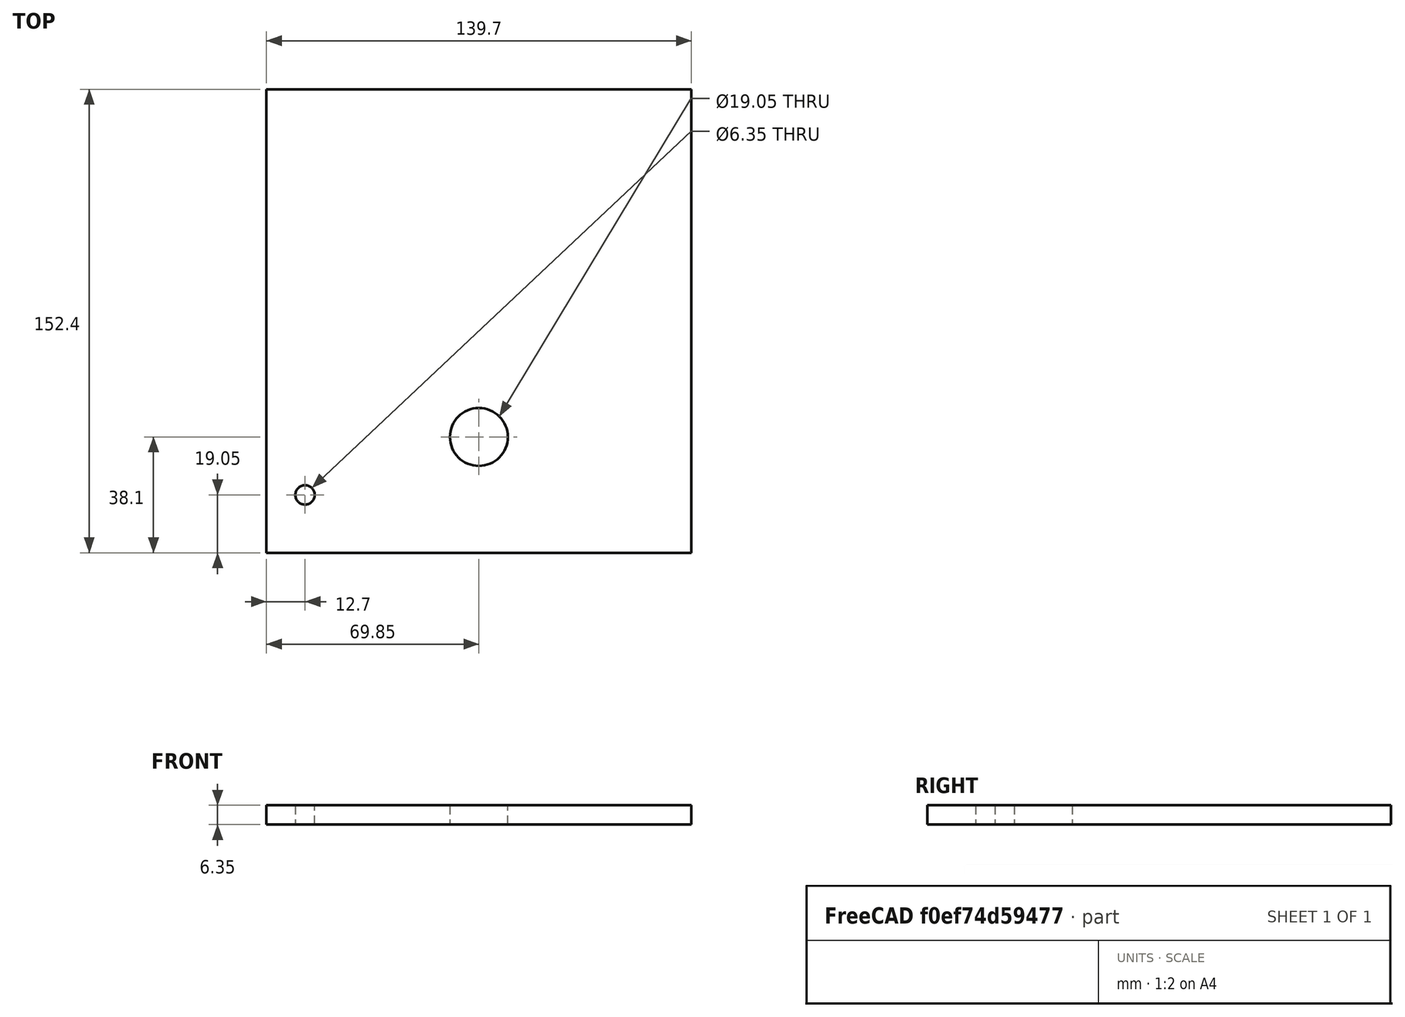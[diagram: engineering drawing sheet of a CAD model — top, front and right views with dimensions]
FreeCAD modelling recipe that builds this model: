
FCSTD DOCUMENT  (FreeCAD 0.22R36784 (Git))
Label: fiat 125 battery cutoff switch plate
License: All rights reserved
LicenseURL: http://en.wikipedia.org/wiki/All_rights_reserved
objects: Sketcher::SketchObject×1, PartDesign::Pad×1, PartDesign::Body×1
note: 4 computed .brp shape members not serialized (recipe doc carries the construction recipe); baked Part::Feature solids carry a one-line shape summary decoded from their .brp

FEATURE [Sketcher::SketchObject] Sketch
  AttachmentSupport = -> [XY_Plane]
  FullyConstrained = true
  MapMode = 5
  sketch-geometry (6):
    g0: LineSegment StartX=0 StartY=0 StartZ=0 EndX=139.7 EndY=0 EndZ=0
    g1: LineSegment StartX=139.7 StartY=0 StartZ=0 EndX=139.7 EndY=152.4 EndZ=0
    g2: LineSegment StartX=139.7 StartY=152.4 StartZ=0 EndX=0 EndY=152.4 EndZ=0
    g3: LineSegment StartX=0 StartY=152.4 StartZ=0 EndX=0 EndY=0 EndZ=0
    g4: Circle CenterX=12.7 CenterY=19.05 CenterZ=0 NormalX=0 NormalY=0 NormalZ=1 AngleXU=0 Radius=3.175
    g5: Circle CenterX=69.85 CenterY=38.1 CenterZ=0 NormalX=0 NormalY=0 NormalZ=1 AngleXU=0 Radius=9.525
  constraints (17):
    c: Coincident(g0,g1)
    c: Coincident(g1,g2)
    c: Coincident(g2,g3)
    c: Coincident(g3,g0)
    c: Horizontal(g0)
    c: Horizontal(g2)
    c: Vertical(g1)
    c: Vertical(g3)
    c: Distance(g1,g3) = 139.7
    c: Distance(g0,g2) = 152.4
    c: Coincident(g0,g-1)
    c: Diameter(g4) = 6.35
    c: DistanceX(g-1,g4) = 12.7
    c: DistanceY(g-1,g4) = 19.05
    c: DistanceX(g-1,g5) = 69.85
    c: DistanceY(g-1,g5) = 38.1
    c: Diameter(g5) = 19.05
FEATURE [PartDesign::Pad] Pad
  Direction = (0,0,1)
  Length = 6.35
  Length2 = 10
  Profile = -> Sketch
  ReferenceAxis = -> Sketch [N_Axis]
  Suppressed = false
  Type = 0
FEATURE [PartDesign::Body] Body
  Group = -> [Sketch,Pad]
  Origin = -> Origin
  Tip = -> Pad
